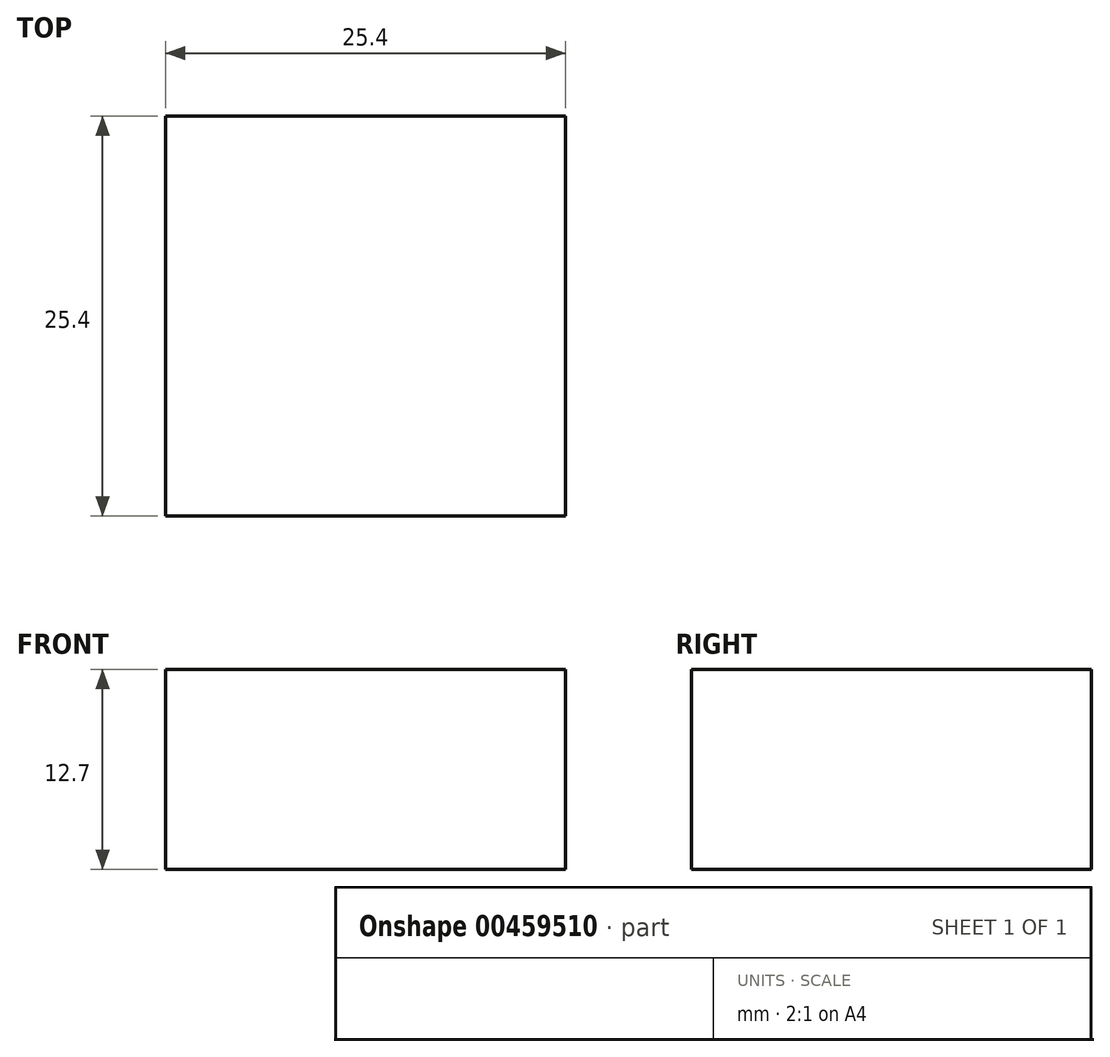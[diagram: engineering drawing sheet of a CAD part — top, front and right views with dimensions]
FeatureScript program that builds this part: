
annotation { "Feature Type Name" : "Feature", "Feature Type Description" : "" }
export const myFeature = defineFeature(function(context is Context, id is Id, definition is map)
    precondition{}
    {
        {
            var Q0;
            Q0=qCreatedBy(makeId("Top.planeOp"),FACE);
            var sketch = newSketch(context, id + "F0", { "sketchPlane" : qUnion([Q0])});
            skLineSegment(sketch, "E0.bottom", {"start": v(-13.13, 15.16) * mm, "end": v(12.27, 15.16) * mm});
            skLineSegment(sketch, "E0.top", {"start": v(-13.13, -10.24) * mm, "end": v(12.27, -10.24) * mm});
            skLineSegment(sketch, "E0.left", {"start": v(-13.13, 15.16) * mm, "end": v(-13.13, -10.24) * mm});
            skLineSegment(sketch, "E0.right", {"start": v(12.27, 15.16) * mm, "end": v(12.27, -10.24) * mm});
            skSolve(sketch);
        }
        {
            var Q0;
            Q0=makeQuery(id+"F0.imprint","IMPRINT",FACE,{"disambiguationData":[TD([[makeQuery(id+"F0.imprint","IMPRINT",EDGE,{"derivedFrom":sQuery(id+"F0.wireOp",EDGE,"E0.bottom")}),-1.0]])]});
            extrude(context, id + "F1", {"entities" : qUnion([Q0]), "depth" : 12.7 * mm});
        }
    });
